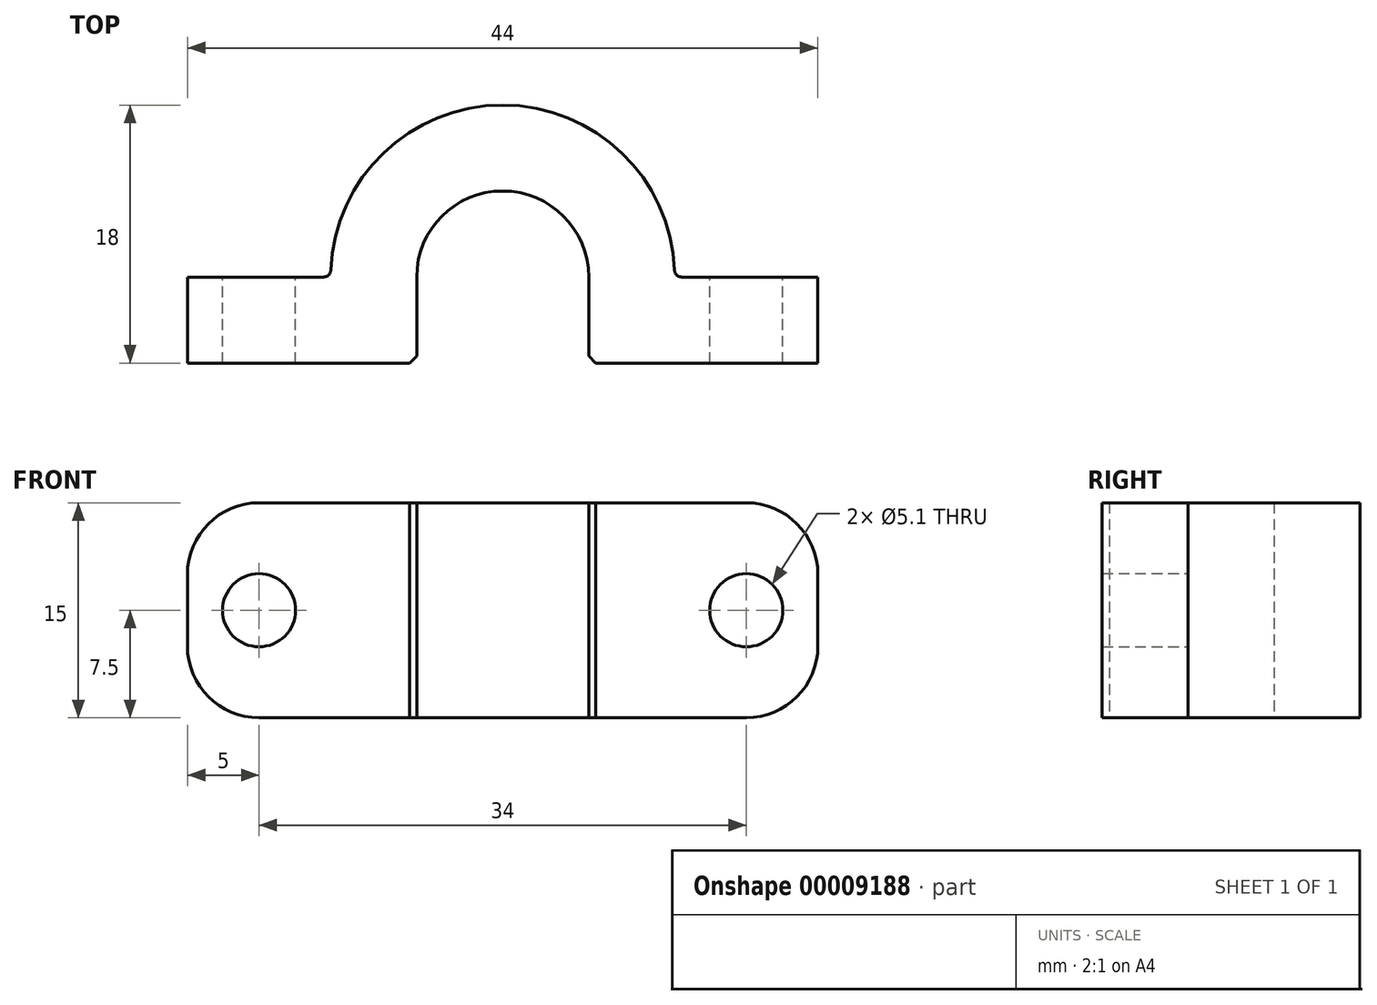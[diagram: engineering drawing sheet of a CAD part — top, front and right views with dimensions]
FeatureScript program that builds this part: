
annotation { "Feature Type Name" : "Feature", "Feature Type Description" : "" }
export const myFeature = defineFeature(function(context is Context, id is Id, definition is map)
    precondition{}
    {
        {
            var Q0;
            Q0=qCreatedBy(makeId("Top.planeOp"),FACE);
            var sketch = newSketch(context, id + "F0", { "sketchPlane" : qUnion([Q0])});
            skArc(sketch, "E0", {"start": v(6, 0) * mm, "mid": v(0, 6) * mm, "end": v(-6, 0) * mm});
            skArc(sketch, "E1", {"start": v(12, 0) * mm, "mid": v(0, 12) * mm, "end": v(-12, 0) * mm});
            skLineSegment(sketch, "E2", {"start": v(12, 0) * mm, "end": v(22, 0) * mm});
            skLineSegment(sketch, "E3", {"start": v(22, 0) * mm, "end": v(22, -6) * mm});
            skLineSegment(sketch, "E4", {"start": v(22, -6) * mm, "end": v(6, -6) * mm});
            skLineSegment(sketch, "E5", {"start": v(-22, -6) * mm, "end": v(-22, 0) * mm});
            skLineSegment(sketch, "E6", {"start": v(-22, 0) * mm, "end": v(-12, 0) * mm});
            skLineSegment(sketch, "E7.trimOffspring", {"start": v(-6, -6) * mm, "end": v(-22, -6) * mm});
            skLineSegment(sketch, "E8", {"start": v(-6, 0) * mm, "end": v(-6, -6) * mm});
            skLineSegment(sketch, "E9", {"start": v(6, 0) * mm, "end": v(6, -6) * mm});
            skSolve(sketch);
        }
        {
            var Q0;
            Q0 = qSketchRegion(id + "F0", true);
            extrude(context, id + "F1", {"entities" : qUnion([Q0]), "depth" : 15 * mm});
        }
        {
            var Q0;
            Q0=makeQuery(id+"F1.opExtrude","SWEPT_FACE",FACE,{"disambiguationData":[OSD([sQuery(id+"F0.wireOp",EDGE,"E6")])]});
            var sketch = newSketch(context, id + "F2", { "sketchPlane" : qUnion([Q0])});
            skCircle(sketch, "E10", {"center": v(17, 7.5) * mm, "radius": 2.55 * mm});
            skCircle(sketch, "E11", {"center": v(-17, 7.5) * mm, "radius": 2.55 * mm});
            skSolve(sketch);
        }
        {
            var Q0;
            Q0 = qSketchRegion(id + "F2", true);
            extrude(context, id + "F3", {"entities" : qUnion([Q0]), "operationType" : NewBodyOperationType.REMOVE, "endBound" : BoundingType.THROUGH_ALL, "oppositeDirection" : true, "depth" : 25 * mm});
        }
        {
            var Q0;
            Q0=makeQuery(id+"F1.opExtrude","SWEPT_EDGE",EDGE,{"disambiguationData":[OSD([sQuery(id+"F0.wireOp",EDGE,"E1"),sQuery(id+"F0.wireOp",EDGE,"E2")])]});
            var Q1;
            Q1=makeQuery(id+"F1.opExtrude","SWEPT_EDGE",EDGE,{"disambiguationData":[OSD([sQuery(id+"F0.wireOp",EDGE,"E1"),sQuery(id+"F0.wireOp",EDGE,"E6")])]});
            fillet(context, id + "F4", {"entities" : qUnion([Q0, Q1]), "radius" : .5 * mm, "tangentPropagation" : true, "allowEdgeOverflow" : false});
        }
        {
            var Q0;
            Q0=makeQuery(id+"F1.opExtrude","SWEPT_EDGE",EDGE,{"disambiguationData":[OSD([sQuery(id+"F0.wireOp",EDGE,"E7.trimOffspring"),sQuery(id+"F0.wireOp",EDGE,"E8")])]});
            var Q1;
            Q1=makeQuery(id+"F1.opExtrude","SWEPT_EDGE",EDGE,{"disambiguationData":[OSD([sQuery(id+"F0.wireOp",EDGE,"E4"),sQuery(id+"F0.wireOp",EDGE,"E9")])]});
            chamfer(context, id + "F5", {"entities" : qUnion([Q0, Q1]), "width" : .5 * mm, "tangentPropagation" : true});
        }
        {
            var Q0;
            Q0=makeQuery(id+"F1.opExtrude","CAP_EDGE",EDGE,{"disambiguationData":[OSD([sQuery(id+"F0.wireOp",EDGE,"E3")])],"isStart":false});
            var Q1;
            Q1=makeQuery(id+"F1.opExtrude","CAP_EDGE",EDGE,{"disambiguationData":[OSD([sQuery(id+"F0.wireOp",EDGE,"E3")])],"isStart":true});
            var Q2;
            Q2=makeQuery(id+"F1.opExtrude","CAP_EDGE",EDGE,{"disambiguationData":[OSD([sQuery(id+"F0.wireOp",EDGE,"E5")])],"isStart":false});
            var Q3;
            Q3=makeQuery(id+"F1.opExtrude","CAP_EDGE",EDGE,{"disambiguationData":[OSD([sQuery(id+"F0.wireOp",EDGE,"E5")])],"isStart":true});
            fillet(context, id + "F6", {"entities" : qUnion([Q0, Q1, Q2, Q3]), "radius" : 5 * mm, "tangentPropagation" : true, "allowEdgeOverflow" : false});
        }
    });
